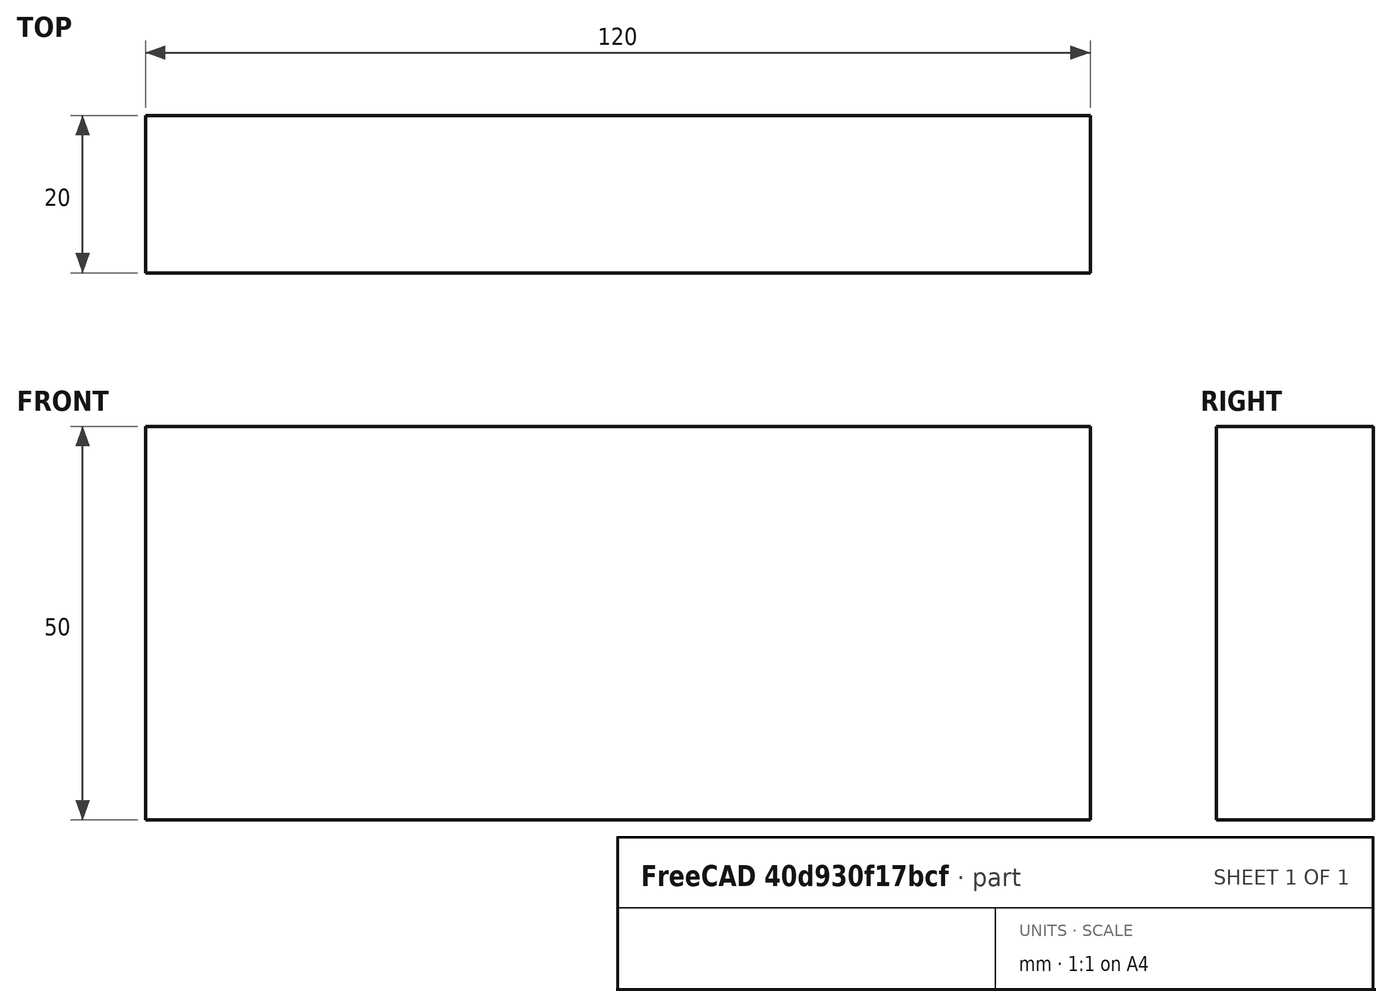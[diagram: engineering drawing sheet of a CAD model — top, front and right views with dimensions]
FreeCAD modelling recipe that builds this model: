
FCSTD DOCUMENT  (FreeCAD 0.15R4671 (Git))
Label: Flat Bar 120x20 EN10058 S235JR
License: All rights reserved
LicenseURL: http://en.wikipedia.org/wiki/All_rights_reserved
objects: Sketcher::SketchObject×1, Part::Extrusion×1
note: 2 computed .brp shape members not serialized (recipe doc carries the construction recipe); baked Part::Feature solids carry a one-line shape summary decoded from their .brp

FEATURE [Sketcher::SketchObject] Sketch
  sketch-geometry (4):
    g0: LineSegment StartX=-60 StartY=-10 StartZ=0 EndX=60 EndY=-10 EndZ=0
    g1: LineSegment StartX=60 StartY=-10 StartZ=0 EndX=60 EndY=10 EndZ=0
    g2: LineSegment StartX=60 StartY=10 StartZ=0 EndX=-60 EndY=10 EndZ=0
    g3: LineSegment StartX=-60 StartY=10 StartZ=0 EndX=-60 EndY=-10 EndZ=0
  constraints (12):
    c: Coincident(g0,g1)
    c: Coincident(g1,g2)
    c: Coincident(g2,g3)
    c: Coincident(g3,g0)
    c: Horizontal(g0)
    c: Horizontal(g2)
    c: Vertical(g1)
    c: Vertical(g3)
    c: Symmetric(g1,g2,g-2)
    c: Symmetric(g0,g1,g-1)
    c: DistanceY(g1) = 20
    c: DistanceX(g0) = 120
FEATURE [Part::Extrusion] Extrude  label="Flat Bar 120x20 EN10058 S235JR"
  Base = -> Sketch
  Dir = (0,0,50)
  Solid = true
